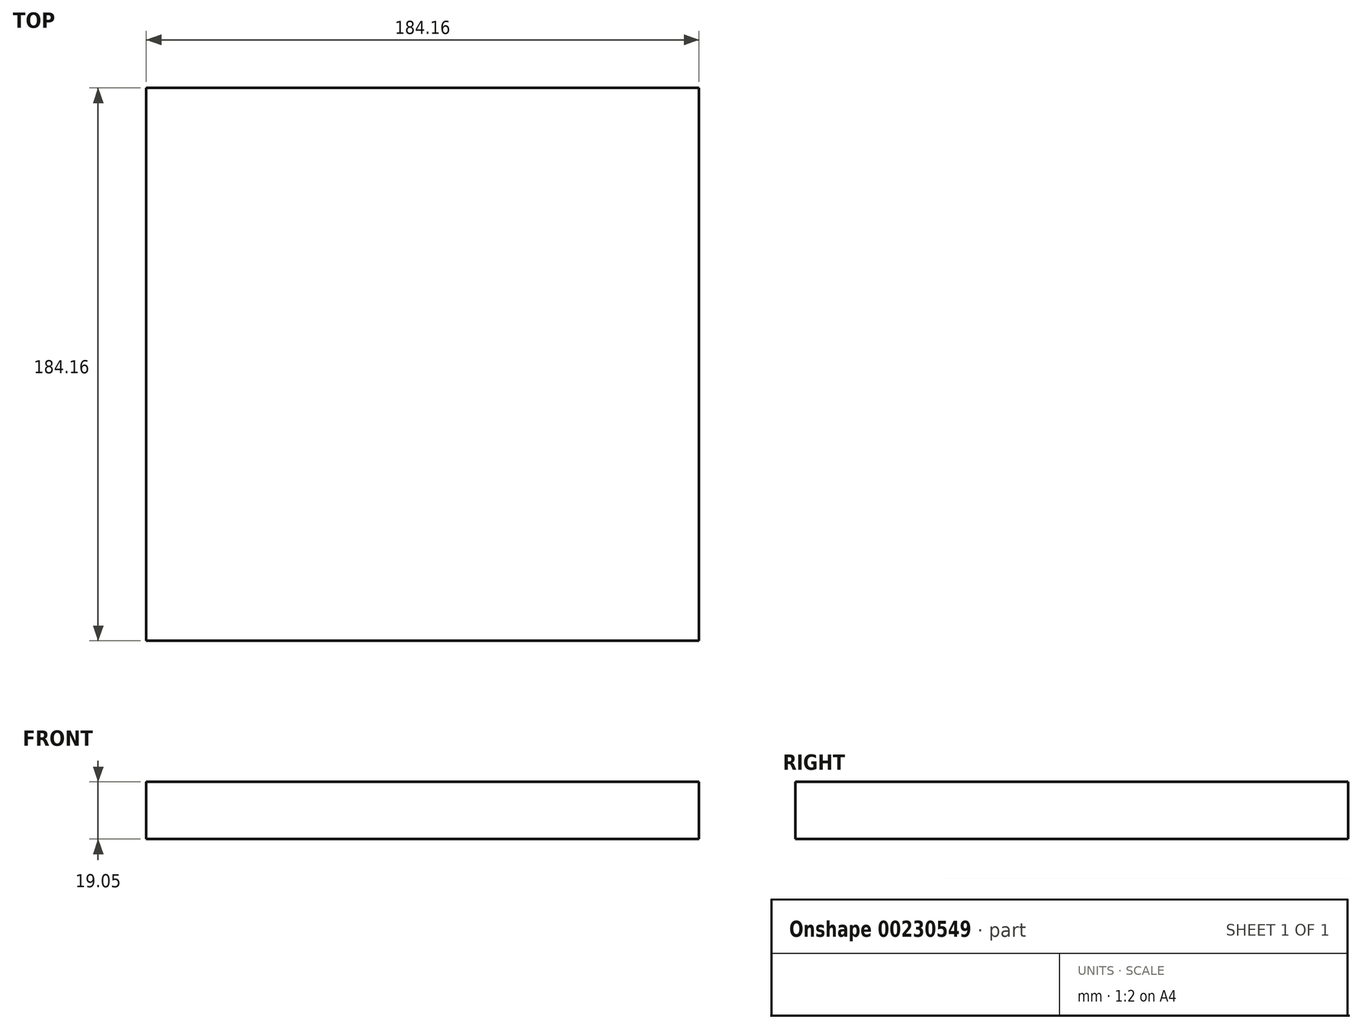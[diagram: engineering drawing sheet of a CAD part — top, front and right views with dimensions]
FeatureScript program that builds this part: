
annotation { "Feature Type Name" : "Feature", "Feature Type Description" : "" }
export const myFeature = defineFeature(function(context is Context, id is Id, definition is map)
    precondition{}
    {
        {
            var Q0;
            Q0=qCreatedBy(makeId("Top.planeOp"),FACE);
            var sketch = newSketch(context, id + "F0", { "sketchPlane" : qUnion([Q0])});
            skLineSegment(sketch, "E0.bottom", {"start": v(92.08, 92.08) * mm, "end": v(-92.08, 92.08) * mm});
            skLineSegment(sketch, "E0.top", {"start": v(92.08, -92.07) * mm, "end": v(-92.08, -92.07) * mm});
            skLineSegment(sketch, "E0.left", {"start": v(92.08, 92.08) * mm, "end": v(92.08, -92.07) * mm});
            skLineSegment(sketch, "E0.right", {"start": v(-92.08, 92.08) * mm, "end": v(-92.08, -92.07) * mm});
            skPoint(sketch, "E0.middle", {"position": v(0, 0) * mm});
            skSolve(sketch);
        }
        {
            var Q0;
            Q0 = qSketchRegion(id + "F0", true);
            extrude(context, id + "F1", {"entities" : qUnion([Q0]), "depth" : 19.05 * mm});
        }
    });
